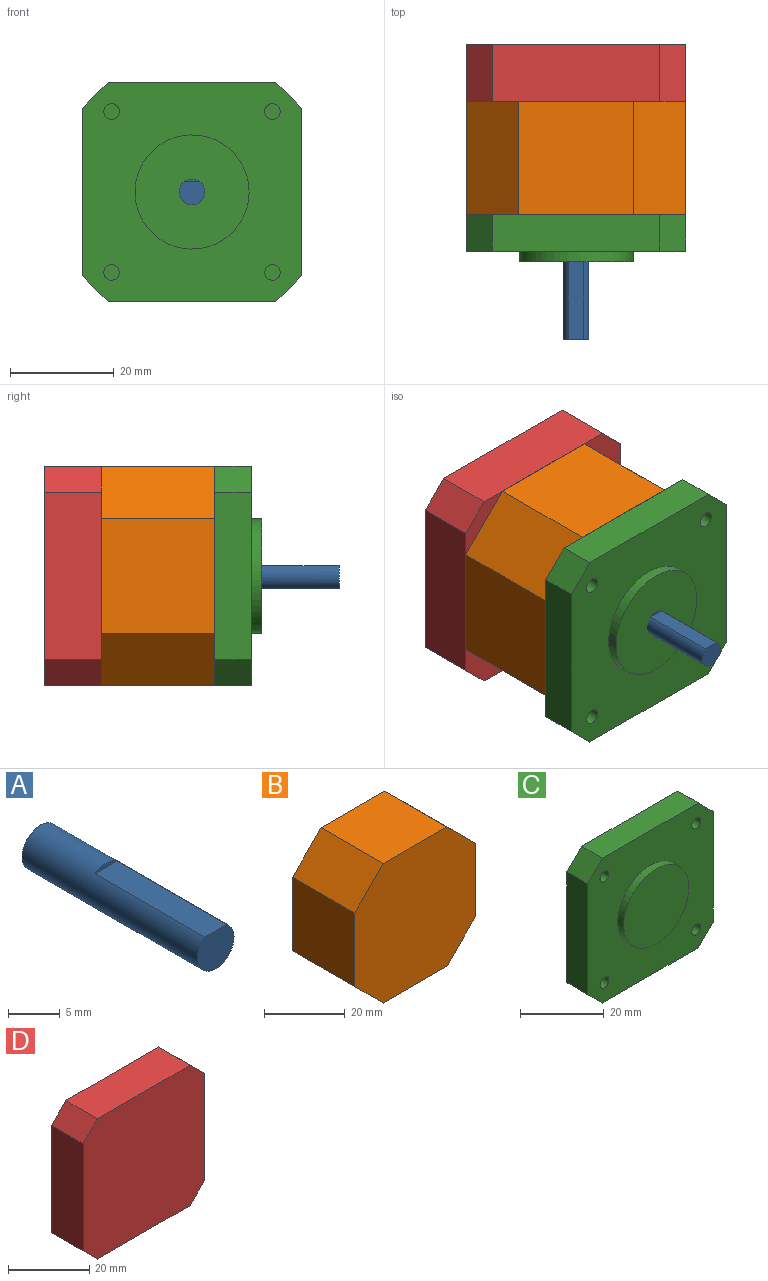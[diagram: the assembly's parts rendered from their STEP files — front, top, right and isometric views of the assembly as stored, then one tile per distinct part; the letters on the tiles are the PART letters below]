
ASSEMBLY  parts=4 mates=3
PART A: 5 faces, bbox 5x24x5 mm
  f0: cylinder r=2.5mm len=24mm, axis (0,1,0), area 328.7mm2, adj f1,f2,f3,f4
  f1: plane 5x4.5mm, normal (0,-1,0), area 18.6mm2, adj f0,f3
  f2: plane 5x5mm, normal (0,1,0), area 19.6mm2, adj f0
  f3: plane 15x3mm, normal (0,0,1), area 45mm2, adj f0,f1,f4
  f4: plane 3x0.5mm, normal (0,-1,0), area 1mm2, adj f0,f3
PART B: 10 faces, bbox 42.3x21.8x42.3 mm
  f0: plane 22.3x21.8mm, normal (1,0,0), area 486.1mm2, adj f4,f5,f8,f9
  f1: plane 22.3x21.8mm, normal (0,0,-1), area 486.1mm2, adj f4,f5,f6,f9
  f2: plane 22.3x21.8mm, normal (-1,0,0), area 486.1mm2, adj f4,f5,f6,f7
  f3: plane 22.3x21.8mm, normal (0,0,1), area 486.1mm2, adj f4,f5,f7,f8
  f4: plane 42.3x42.3mm, normal (0,1,0), area 1589.3mm2, adj f0,f1,f2,f3,f6,f7,f8,f9
  f5: plane 42.3x42.3mm, normal (0,-1,0), area 1589.3mm2, adj f0,f1,f2,f3,f6,f7,f8,f9
  f6: plane 21.8x10mm, normal (-0.71,0,-0.71), area 308.3mm2, adj f1,f2,f4,f5
  f7: plane 21.8x10mm, normal (-0.71,0,0.71), area 308.3mm2, adj f2,f3,f4,f5
  f8: plane 21.8x10mm, normal (0.71,0,0.71), area 308.3mm2, adj f0,f3,f4,f5
  f9: plane 21.8x10mm, normal (0.71,0,-0.71), area 308.3mm2, adj f0,f1,f4,f5
PART C: 20 faces, bbox 42.3x9x42.3 mm
  f0: plane 42.3x42.3mm, normal (0,-1,0), area 1330.9mm2, adj f1,f2,f3,f4,f6,f7,f8,f9
  f1: plane 32.3x7mm, normal (-1,0,0), area 226.1mm2, adj f0,f5,f6,f9
  f2: plane 32.3x7mm, normal (0,0,-1), area 226.1mm2, adj f0,f5,f6,f7
  f3: plane 32.3x7mm, normal (1,0,0), area 226.1mm2, adj f0,f5,f7,f8
  f4: plane 32.3x7mm, normal (0,0,1), area 226.1mm2, adj f0,f5,f8,f9
  f5: plane 42.3x42.3mm, normal (0,1,0), area 1739.3mm2, adj f1,f2,f3,f4,f6,f7,f8,f9
  f6: plane 7x5mm, normal (-0.71,0,-0.71), area 49.5mm2, adj f0,f1,f2,f5
  f7: plane 7x5mm, normal (0.71,0,-0.71), area 49.5mm2, adj f0,f2,f3,f5
  f8: plane 7x5mm, normal (0.71,0,0.71), area 49.5mm2, adj f0,f3,f4,f5
  f9: plane 7x5mm, normal (-0.71,0,0.71), area 49.5mm2, adj f0,f1,f4,f5
  f10: cylinder r=11mm len=22mm, axis (0,1,0), area 138.2mm2, adj f0,f11
  f11: plane 22x22mm, normal (0,-1,0), area 380.1mm2, adj f10
  f12: cylinder r=1.5mm len=4.5mm, axis (0,-1,0), area 42.4mm2, adj f0,f13
  f13: plane 3x3mm, normal (0,-1,0), area 7.1mm2, adj f12
  f14: cylinder r=1.5mm len=4.5mm, axis (0,-1,0), area 42.4mm2, adj f0,f15
  f15: plane 3x3mm, normal (0,-1,0), area 7.1mm2, adj f14
  f16: cylinder r=1.5mm len=4.5mm, axis (0,-1,0), area 42.4mm2, adj f0,f17
  f17: plane 3x3mm, normal (0,-1,0), area 7.1mm2, adj f16
  f18: cylinder r=1.5mm len=4.5mm, axis (0,-1,0), area 42.4mm2, adj f0,f19
  f19: plane 3x3mm, normal (0,-1,0), area 7.1mm2, adj f18
PART D: 18 faces, bbox 42.3x11x42.3 mm
  f0: plane 32.3x11mm, normal (1,0,0), area 355.3mm2, adj f4,f5,f8,f9
  f1: plane 32.3x11mm, normal (0,0,-1), area 355.3mm2, adj f4,f5,f7,f8
  f2: plane 32.3x11mm, normal (-1,0,0), area 355.3mm2, adj f4,f5,f6,f7
  f3: plane 32.3x11mm, normal (0,0,1), area 355.3mm2, adj f4,f5,f6,f9
  f4: plane 42.3x42.3mm, normal (0,1,0), area 1711mm2, adj f0,f1,f2,f3,f6,f7,f8,f9
  f5: plane 42.3x42.3mm, normal (0,-1,0), area 1739.3mm2, adj f0,f1,f2,f3,f6,f7,f8,f9
  f6: plane 11x5mm, normal (-0.71,0,0.71), area 77.8mm2, adj f2,f3,f4,f5
  f7: plane 11x5mm, normal (-0.71,0,-0.71), area 77.8mm2, adj f1,f2,f4,f5
  f8: plane 11x5mm, normal (0.71,0,-0.71), area 77.8mm2, adj f0,f1,f4,f5
  f9: plane 11x5mm, normal (0.71,0,0.71), area 77.8mm2, adj f0,f3,f4,f5
  f10: cylinder r=1.5mm len=4.5mm, axis (0,1,0), area 42.4mm2, adj f4,f11
  f11: plane 3x3mm, normal (0,1,0), area 7.1mm2, adj f10
  f12: cylinder r=1.5mm len=4.5mm, axis (0,1,0), area 42.4mm2, adj f4,f13
  f13: plane 3x3mm, normal (0,1,0), area 7.1mm2, adj f12
  f14: cylinder r=1.5mm len=4.5mm, axis (0,1,0), area 42.4mm2, adj f4,f15
  f15: plane 3x3mm, normal (0,1,0), area 7.1mm2, adj f14
  f16: cylinder r=1.5mm len=4.5mm, axis (0,1,0), area 42.4mm2, adj f4,f17
  f17: plane 3x3mm, normal (0,1,0), area 7.1mm2, adj f16
PLACE A t=(0,24,0)mm
PLACE B t=(0,15,0)mm
PLACE C t=(0,15,0)mm
PLACE D t=(0,15,0)mm
MATE fastened C.f10 <-> B.f5  axis (0,1,0) through (0,24,0)mm
MATE fastened A.f0 <-> B.f5  axis (0,1,0) through (0,24,0)mm
MATE fastened D.f5 <-> B.f4  axis (0,-1,0) through (0,45.8,0)mm
